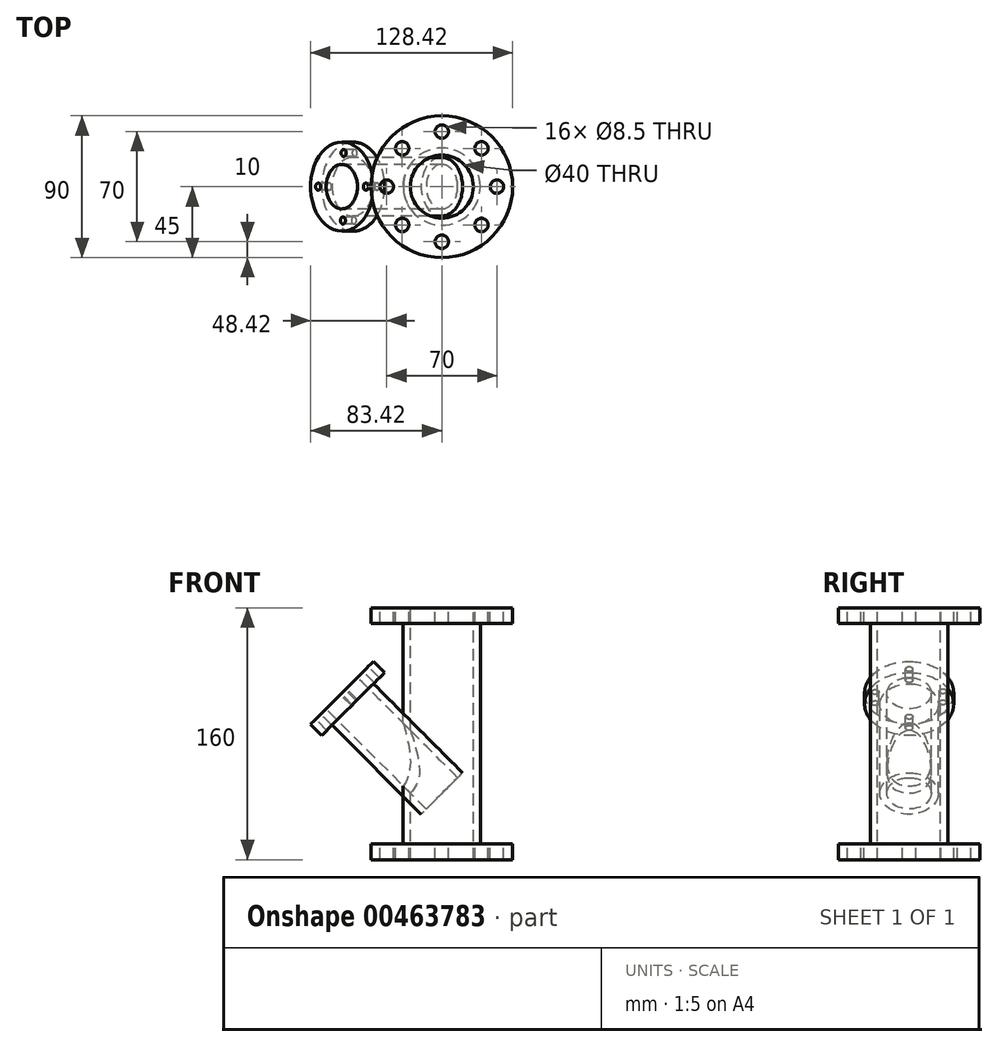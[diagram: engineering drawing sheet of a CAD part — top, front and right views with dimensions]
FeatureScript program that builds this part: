
annotation { "Feature Type Name" : "Feature", "Feature Type Description" : "" }
export const myFeature = defineFeature(function(context is Context, id is Id, definition is map)
    precondition{}
    {
        {
            var Q0;
            Q0=qCreatedBy(makeId("Top.planeOp"),FACE);
            var sketch = newSketch(context, id + "F0", { "sketchPlane" : qUnion([Q0])});
            skCircle(sketch, "E0", {"center": v(0, 0) * mm, "radius": 45 * mm});
            skSolve(sketch);
        }
        {
            var Q0;
            Q0 = qSketchRegion(id + "F0", true);
            extrude(context, id + "F1", {"entities" : qUnion([Q0]), "depth" : 10 * mm});
        }
        {
            var Q0;
            Q0=makeQuery(id+"F1.opExtrude","CAP_FACE",FACE,{"disambiguationData":[OSD([sQuery(id+"F0.wireOp",EDGE,"E0")])],"isStart":true});
            var sketch = newSketch(context, id + "F2", { "sketchPlane" : qUnion([Q0])});
            skCircle(sketch, "E1", {"center": v(0, 0) * mm, "radius": 24.5 * mm});
            skCircle(sketch, "E2", {"center": v(0, 0) * mm, "radius": 20 * mm});
            skSolve(sketch);
        }
        {
            var Q0;
            Q0 = qSketchRegion(id + "F2", true);
            extrude(context, id + "F3", {"entities" : qUnion([Q0]), "operationType" : NewBodyOperationType.ADD, "depth" : 140 * mm});
        }
        {
            var Q0;
            Q0=makeQuery(id+"F1.opExtrude","CAP_FACE",FACE,{"disambiguationData":[OSD([sQuery(id+"F0.wireOp",EDGE,"E0")])],"isStart":false});
            var sketch = newSketch(context, id + "F4", { "sketchPlane" : qUnion([Q0])});
            skCircle(sketch, "E3", {"center": v(0, 0) * mm, "radius": 20 * mm});
            skSolve(sketch);
        }
        {
            var Q0;
            Q0 = qSketchRegion(id + "F4", true);
            extrude(context, id + "F5", {"entities" : qUnion([Q0]), "operationType" : NewBodyOperationType.REMOVE, "endBound" : BoundingType.THROUGH_ALL, "oppositeDirection" : true, "depth" : 25 * mm});
        }
        {
            var Q0;
            Q0=qCreatedBy(makeId("Top.planeOp"),FACE);
            var sketch = newSketch(context, id + "F6", { "sketchPlane" : qUnion([Q0])});
            skCircle(sketch, "E4", {"center": v(0, 0) * mm, "radius": 45 * mm});
            skCircle(sketch, "E5", {"center": v(0, 0) * mm, "radius": 20 * mm});
            skSolve(sketch);
        }
        {
            var Q0;
            Q0 = qSketchRegion(id + "F6", true);
            extrude(context, id + "F7", {"entities" : qUnion([Q0]), "operationType" : NewBodyOperationType.ADD, "depth" : 10 * mm});
        }
        {
            var Q0;
            Q0=makeQuery(id+"F3.opExtrude","CAP_FACE",FACE,{"disambiguationData":[OSD([sQuery(id+"F2.wireOp",EDGE,"E1"),sQuery(id+"F2.wireOp",EDGE,"E2")])],"isStart":false});
            var sketch = newSketch(context, id + "F8", { "sketchPlane" : qUnion([Q0])});
            skCircle(sketch, "E6", {"center": v(0, 0) * mm, "radius": 45 * mm});
            skCircle(sketch, "E7", {"center": v(0, 0) * mm, "radius": 20 * mm});
            skSolve(sketch);
        }
        {
            var Q0;
            Q0 = qSketchRegion(id + "F8", true);
            extrude(context, id + "F9", {"entities" : qUnion([Q0]), "operationType" : NewBodyOperationType.ADD, "depth" : 10 * mm});
        }
        {
            var Q0;
            Q0=makeQuery(id+"F1.opExtrude","CAP_FACE",FACE,{"disambiguationData":[OSD([sQuery(id+"F0.wireOp",EDGE,"E0")])],"isStart":false});
            var sketch = newSketch(context, id + "F10", { "sketchPlane" : qUnion([Q0])});
            skCircle(sketch, "E8", {"center": v(0, 0) * mm, "radius": 35 * mm});
            skCircle(sketch, "E9", {"center": v(0, 35) * mm, "radius": 4.25 * mm});
            skCircle(sketch, "E10", {"center": v(0, -35) * mm, "radius": 4.25 * mm});
            skCircle(sketch, "E11", {"center": v(35, 0) * mm, "radius": 4.25 * mm});
            skCircle(sketch, "E12", {"center": v(-35, 0) * mm, "radius": 4.25 * mm});
            skCircle(sketch, "E13", {"center": v(-25.17, 24.32) * mm, "radius": 4.25 * mm});
            skCircle(sketch, "E14", {"center": v(25.17, 24.32) * mm, "radius": 4.25 * mm});
            skCircle(sketch, "E15", {"center": v(25.17, -24.32) * mm, "radius": 4.25 * mm});
            skCircle(sketch, "E16", {"center": v(-25.17, -24.32) * mm, "radius": 4.25 * mm});
            skSolve(sketch);
        }
        {
            var Q0;
            Q0=makeQuery(id+"F10.imprint","IMPRINT",FACE,{"disambiguationData":[TD([[makeQuery(id+"F10.imprint","IMPRINT",EDGE,{"derivedFrom":makeQuery(id+"F5.boolean.opBoolean","COPY",EDGE,{"derivedFrom":makeQuery(id+"F5.opExtrude","CAP_EDGE",EDGE,{"disambiguationData":[OSD([sQuery(id+"F4.wireOp",EDGE,"E3")])],"isStart":true})})}),1.0]])]});
            var Q1;
            {var subQ0=sQuery(id+"F10.wireOp",EDGE,"E14");var subQ1=sQuery(id+"F10.wireOp",EDGE,"E8");var subQ2=makeQuery(id+"F10.imprint","INTERSECT",VERTEX,{"disambiguationData":[OD(0.0)],"derivedFrom":[subQ1,subQ0]});Q1=makeQuery(id+"F10.imprint","IMPRINT",FACE,{"disambiguationData":[TD([[makeQuery(id+"F10.imprint","IMPRINT",EDGE,{"disambiguationData":[TD([[subQ2,-1.0]])],"derivedFrom":subQ1}),1.0]])]});}
            var Q2;
            {var subQ0=sQuery(id+"F10.wireOp",EDGE,"E14");var subQ1=sQuery(id+"F10.wireOp",EDGE,"E8");var subQ2=makeQuery(id+"F10.imprint","INTERSECT",VERTEX,{"disambiguationData":[OD(0.0)],"derivedFrom":[subQ1,subQ0]});Q2=makeQuery(id+"F10.imprint","IMPRINT",FACE,{"disambiguationData":[TD([[makeQuery(id+"F10.imprint","IMPRINT",EDGE,{"disambiguationData":[TD([[subQ2,-1.0]])],"derivedFrom":subQ1}),-1.0]])]});}
            var Q3;
            {var subQ0=sQuery(id+"F10.wireOp",EDGE,"E9");var subQ1=sQuery(id+"F10.wireOp",EDGE,"E8");var subQ2=makeQuery(id+"F10.imprint","INTERSECT",VERTEX,{"disambiguationData":[OD(0.0)],"derivedFrom":[subQ1,subQ0]});Q3=makeQuery(id+"F10.imprint","IMPRINT",FACE,{"disambiguationData":[TD([[makeQuery(id+"F10.imprint","IMPRINT",EDGE,{"disambiguationData":[TD([[subQ2,-1.0]])],"derivedFrom":subQ1}),1.0]])]});}
            var Q4;
            {var subQ0=sQuery(id+"F10.wireOp",EDGE,"E9");var subQ1=sQuery(id+"F10.wireOp",EDGE,"E8");var subQ2=makeQuery(id+"F10.imprint","INTERSECT",VERTEX,{"disambiguationData":[OD(0.0)],"derivedFrom":[subQ1,subQ0]});Q4=makeQuery(id+"F10.imprint","IMPRINT",FACE,{"disambiguationData":[TD([[makeQuery(id+"F10.imprint","IMPRINT",EDGE,{"disambiguationData":[TD([[subQ2,-1.0]])],"derivedFrom":subQ1}),-1.0]])]});}
            var Q5;
            {var subQ0=sQuery(id+"F10.wireOp",EDGE,"E13");var subQ1=sQuery(id+"F10.wireOp",EDGE,"E8");var subQ2=makeQuery(id+"F10.imprint","INTERSECT",VERTEX,{"disambiguationData":[OD(0.0)],"derivedFrom":[subQ1,subQ0]});Q5=makeQuery(id+"F10.imprint","IMPRINT",FACE,{"disambiguationData":[TD([[makeQuery(id+"F10.imprint","IMPRINT",EDGE,{"disambiguationData":[TD([[subQ2,-1.0]])],"derivedFrom":subQ1}),-1.0]])]});}
            var Q6;
            {var subQ0=sQuery(id+"F10.wireOp",EDGE,"E13");var subQ1=sQuery(id+"F10.wireOp",EDGE,"E8");var subQ2=makeQuery(id+"F10.imprint","INTERSECT",VERTEX,{"disambiguationData":[OD(0.0)],"derivedFrom":[subQ1,subQ0]});Q6=makeQuery(id+"F10.imprint","IMPRINT",FACE,{"disambiguationData":[TD([[makeQuery(id+"F10.imprint","IMPRINT",EDGE,{"disambiguationData":[TD([[subQ2,-1.0]])],"derivedFrom":subQ1}),1.0]])]});}
            var Q7;
            {var subQ0=sQuery(id+"F10.wireOp",EDGE,"E12");var subQ1=sQuery(id+"F10.wireOp",EDGE,"E8");var subQ2=makeQuery(id+"F10.imprint","INTERSECT",VERTEX,{"disambiguationData":[OD(0.0)],"derivedFrom":[subQ1,subQ0]});Q7=makeQuery(id+"F10.imprint","IMPRINT",FACE,{"disambiguationData":[TD([[makeQuery(id+"F10.imprint","IMPRINT",EDGE,{"disambiguationData":[TD([[subQ2,-1.0]])],"derivedFrom":subQ1}),-1.0]])]});}
            var Q8;
            {var subQ0=sQuery(id+"F10.wireOp",EDGE,"E12");var subQ1=sQuery(id+"F10.wireOp",EDGE,"E8");var subQ2=makeQuery(id+"F10.imprint","INTERSECT",VERTEX,{"disambiguationData":[OD(0.0)],"derivedFrom":[subQ1,subQ0]});Q8=makeQuery(id+"F10.imprint","IMPRINT",FACE,{"disambiguationData":[TD([[makeQuery(id+"F10.imprint","IMPRINT",EDGE,{"disambiguationData":[TD([[subQ2,-1.0]])],"derivedFrom":subQ1}),1.0]])]});}
            var Q9;
            {var subQ0=sQuery(id+"F10.wireOp",EDGE,"E16");var subQ1=sQuery(id+"F10.wireOp",EDGE,"E8");var subQ2=makeQuery(id+"F10.imprint","INTERSECT",VERTEX,{"disambiguationData":[OD(0.0)],"derivedFrom":[subQ1,subQ0]});Q9=makeQuery(id+"F10.imprint","IMPRINT",FACE,{"disambiguationData":[TD([[makeQuery(id+"F10.imprint","IMPRINT",EDGE,{"disambiguationData":[TD([[subQ2,-1.0]])],"derivedFrom":subQ1}),-1.0]])]});}
            var Q10;
            {var subQ0=sQuery(id+"F10.wireOp",EDGE,"E16");var subQ1=sQuery(id+"F10.wireOp",EDGE,"E8");var subQ2=makeQuery(id+"F10.imprint","INTERSECT",VERTEX,{"disambiguationData":[OD(0.0)],"derivedFrom":[subQ1,subQ0]});Q10=makeQuery(id+"F10.imprint","IMPRINT",FACE,{"disambiguationData":[TD([[makeQuery(id+"F10.imprint","IMPRINT",EDGE,{"disambiguationData":[TD([[subQ2,-1.0]])],"derivedFrom":subQ1}),1.0]])]});}
            var Q11;
            {var subQ0=sQuery(id+"F10.wireOp",EDGE,"E10");var subQ1=sQuery(id+"F10.wireOp",EDGE,"E8");var subQ2=makeQuery(id+"F10.imprint","INTERSECT",VERTEX,{"disambiguationData":[OD(0.0)],"derivedFrom":[subQ1,subQ0]});Q11=makeQuery(id+"F10.imprint","IMPRINT",FACE,{"disambiguationData":[TD([[makeQuery(id+"F10.imprint","IMPRINT",EDGE,{"disambiguationData":[TD([[subQ2,-1.0]])],"derivedFrom":subQ1}),1.0]])]});}
            var Q12;
            {var subQ0=sQuery(id+"F10.wireOp",EDGE,"E10");var subQ1=sQuery(id+"F10.wireOp",EDGE,"E8");var subQ2=makeQuery(id+"F10.imprint","INTERSECT",VERTEX,{"disambiguationData":[OD(0.0)],"derivedFrom":[subQ1,subQ0]});Q12=makeQuery(id+"F10.imprint","IMPRINT",FACE,{"disambiguationData":[TD([[makeQuery(id+"F10.imprint","IMPRINT",EDGE,{"disambiguationData":[TD([[subQ2,-1.0]])],"derivedFrom":subQ1}),-1.0]])]});}
            var Q13;
            {var subQ0=sQuery(id+"F10.wireOp",EDGE,"E15");var subQ1=sQuery(id+"F10.wireOp",EDGE,"E8");var subQ2=makeQuery(id+"F10.imprint","INTERSECT",VERTEX,{"disambiguationData":[OD(0.0)],"derivedFrom":[subQ1,subQ0]});Q13=makeQuery(id+"F10.imprint","IMPRINT",FACE,{"disambiguationData":[TD([[makeQuery(id+"F10.imprint","IMPRINT",EDGE,{"disambiguationData":[TD([[subQ2,-1.0]])],"derivedFrom":subQ1}),1.0]])]});}
            var Q14;
            {var subQ0=sQuery(id+"F10.wireOp",EDGE,"E15");var subQ1=sQuery(id+"F10.wireOp",EDGE,"E8");var subQ2=makeQuery(id+"F10.imprint","INTERSECT",VERTEX,{"disambiguationData":[OD(0.0)],"derivedFrom":[subQ1,subQ0]});Q14=makeQuery(id+"F10.imprint","IMPRINT",FACE,{"disambiguationData":[TD([[makeQuery(id+"F10.imprint","IMPRINT",EDGE,{"disambiguationData":[TD([[subQ2,-1.0]])],"derivedFrom":subQ1}),-1.0]])]});}
            var Q15;
            {var subQ0=sQuery(id+"F10.wireOp",EDGE,"E11");var subQ1=sQuery(id+"F10.wireOp",EDGE,"E8");var subQ2=makeQuery(id+"F10.imprint","INTERSECT",VERTEX,{"disambiguationData":[OD(0.0)],"derivedFrom":[subQ1,subQ0]});Q15=makeQuery(id+"F10.imprint","IMPRINT",FACE,{"disambiguationData":[TD([[makeQuery(id+"F10.imprint","IMPRINT",EDGE,{"disambiguationData":[TD([[subQ2,1.0]])],"derivedFrom":subQ1}),1.0]])]});}
            var Q16;
            {var subQ0=sQuery(id+"F10.wireOp",EDGE,"E11");var subQ1=sQuery(id+"F10.wireOp",EDGE,"E8");var subQ2=makeQuery(id+"F10.imprint","INTERSECT",VERTEX,{"disambiguationData":[OD(0.0)],"derivedFrom":[subQ1,subQ0]});Q16=makeQuery(id+"F10.imprint","IMPRINT",FACE,{"disambiguationData":[TD([[makeQuery(id+"F10.imprint","IMPRINT",EDGE,{"disambiguationData":[TD([[subQ2,1.0]])],"derivedFrom":subQ1}),-1.0]])]});}
            extrude(context, id + "F11", {"entities" : qUnion([Q0, Q1, Q2, Q3, Q4, Q5, Q6, Q7, Q8, Q9, Q10, Q11, Q12, Q13, Q14, Q15, Q16]), "operationType" : NewBodyOperationType.REMOVE, "endBound" : BoundingType.THROUGH_ALL, "oppositeDirection" : true, "depth" : 25 * mm});
        }
        {
            var Q0;
            Q0=qCreatedBy(makeId("Front.planeOp"),FACE);
            var sketch = newSketch(context, id + "F12", { "sketchPlane" : qUnion([Q0])});
            skLineSegment(sketch, "E17", {"start": v(0, -147.03) * mm, "end": v(0, -107.94) * mm});
            skLineSegment(sketch, "E18", {"start": v(0, -107.94) * mm, "end": v(-63.64, -44.3) * mm});
            skLineSegment(sketch, "E19", {"start": v(0, -107.94) * mm, "end": v(0, -74.58) * mm});
            skPoint(sketch, "E20", {"position": v(-43.49, -24.15) * mm});
            skPoint(sketch, "E21", {"position": v(-83.8, -64.45) * mm});
            skLineSegment(sketch, "E22", {"start": v(-43.49, -24.15) * mm, "end": v(-83.8, -64.45) * mm});
            skSolve(sketch);
        }
        {
            var Q0;
            Q0=qCreatedBy(makeId("Right.planeOp"),FACE);
            var Q1;
            Q1=sQuery(id+"F12.wireOp",EDGE,"E22");
            cPlane(context, id + "F13", {"entities" : qUnion([Q0, Q1]), "cplaneType" : CPlaneType.LINE_ANGLE, "offset" : 25 * mm, "angle" : 0 * degree, "width" : 150 * mm, "height" : 150 * mm});
        }
        {
            var Q0;
            Q0=qCreatedBy(id+"F13.planeOp",FACE);
            var sketch = newSketch(context, id + "F14", { "sketchPlane" : qUnion([Q0])});
            skLineSegment(sketch, "E23", {"start": v(0, -47.75) * mm, "end": v(0, -104.94) * mm});
            skCircle(sketch, "E24", {"center": v(0, -76.35) * mm, "radius": 18.6 * mm});
            skSolve(sketch);
        }
        {
            var Q0;
            Q0 = qSketchRegion(id + "F14", true);
            extrude(context, id + "F15", {"entities" : qUnion([Q0]), "oppositeDirection" : true, "depth" : 90 * mm});
        }
        {
            var Q0;
            Q0=qCreatedBy(id+"F13.planeOp",FACE);
            var sketch = newSketch(context, id + "F16", { "sketchPlane" : qUnion([Q0])});
            skCircle(sketch, "E25", {"center": v(0, -76) * mm, "radius": 28.3 * mm});
            skSolve(sketch);
        }
        {
            var Q0;
            Q0 = qSketchRegion(id + "F16", true);
            extrude(context, id + "F17", {"entities" : qUnion([Q0]), "operationType" : NewBodyOperationType.ADD, "oppositeDirection" : true, "depth" : 10 * mm});
        }
        {
            var Q0;
            Q0=qCreatedBy(id+"F13.planeOp",FACE);
            var sketch = newSketch(context, id + "F18", { "sketchPlane" : qUnion([Q0])});
            skCircle(sketch, "E26", {"center": v(0, -76.21) * mm, "radius": 14.1 * mm});
            skSolve(sketch);
        }
        {
            var Q0;
            Q0 = qSketchRegion(id + "F18", true);
            extrude(context, id + "F19", {"entities" : qUnion([Q0]), "operationType" : NewBodyOperationType.REMOVE, "oppositeDirection" : true, "depth" : 90 * mm});
        }
        {
            var Q0;
            Q0=qCreatedBy(id+"F13.planeOp",FACE);
            var sketch = newSketch(context, id + "F20", { "sketchPlane" : qUnion([Q0])});
            skCircle(sketch, "E27", {"center": v(21.47, -75.2) * mm, "radius": 2.25 * mm});
            skCircle(sketch, "E28", {"center": v(0, -54.6) * mm, "radius": 2.25 * mm});
            skCircle(sketch, "E29", {"center": v(0, -97.43) * mm, "radius": 2.25 * mm});
            skCircle(sketch, "E30", {"center": v(-21.45, -74.53) * mm, "radius": 2.25 * mm});
            skSolve(sketch);
        }
        {
            var Q0;
            Q0 = qSketchRegion(id + "F20", true);
            extrude(context, id + "F21", {"entities" : qUnion([Q0]), "operationType" : NewBodyOperationType.REMOVE, "oppositeDirection" : true, "depth" : 25 * mm});
        }
    });
